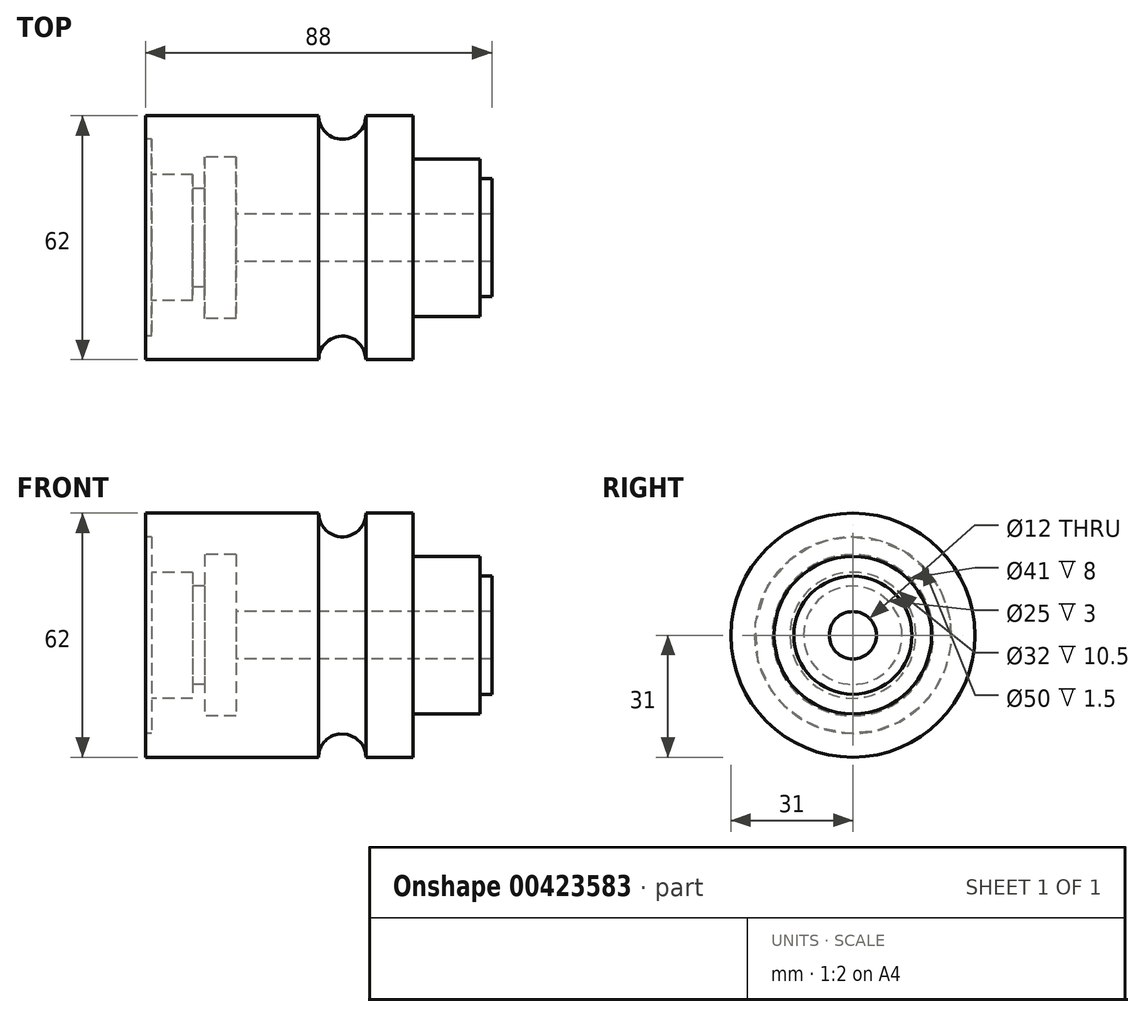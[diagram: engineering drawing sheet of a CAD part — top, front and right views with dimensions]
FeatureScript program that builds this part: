
annotation { "Feature Type Name" : "Feature", "Feature Type Description" : "" }
export const myFeature = defineFeature(function(context is Context, id is Id, definition is map)
    precondition{}
    {
        {
            var Q0;
            Q0=qCreatedBy(makeId("Front.planeOp"),FACE);
            var sketch = newSketch(context, id + "F0", { "sketchPlane" : qUnion([Q0])});
            skLineSegment(sketch, "E0", {"start": v(0, 0) * mm, "end": v(227.58, 0) * mm, "construction": true});
            skLineSegment(sketch, "E1", {"start": v(0, 0) * mm, "end": v(0, 31) * mm});
            skLineSegment(sketch, "E2", {"start": v(0, 31) * mm, "end": v(44, 31) * mm});
            skLineSegment(sketch, "E3", {"start": v(68, 31) * mm, "end": v(68, 20) * mm});
            skLineSegment(sketch, "E4", {"start": v(68, 20) * mm, "end": v(85, 20) * mm});
            skLineSegment(sketch, "E5", {"start": v(85, 20) * mm, "end": v(85, 15) * mm});
            skLineSegment(sketch, "E6", {"start": v(85, 15) * mm, "end": v(88, 15) * mm});
            skLineSegment(sketch, "E7", {"start": v(88, 15) * mm, "end": v(88, 0) * mm});
            skLineSegment(sketch, "E8", {"start": v(88, 0) * mm, "end": v(0, 0) * mm});
            skArc(sketch, "E9", {"start": v(44, 31) * mm, "mid": v(50, 25) * mm, "end": v(56, 31) * mm});
            skLineSegment(sketch, "E10.trimOffspring", {"start": v(56, 31) * mm, "end": v(68, 31) * mm});
            skSolve(sketch);
        }
        {
            var Q0;
            Q0=makeQuery(id+"F0.imprint","IMPRINT",FACE,{"disambiguationData":[TD([[makeQuery(id+"F0.imprint","IMPRINT",EDGE,{"derivedFrom":sQuery(id+"F0.wireOp",EDGE,"E1")}),-1.0]])]});
            var Q1;
            Q1=sQuery(id+"F0.wireOp",EDGE,"E0");
            revolve(context, id + "F1", {"entities" : qUnion([Q0]), "axis" : qUnion([Q1]), "revolveType" : RevolveType.FULL});
        }
        {
            var Q0;
            Q0=qCreatedBy(makeId("Front.planeOp"),FACE);
            var sketch = newSketch(context, id + "F2", { "sketchPlane" : qUnion([Q0])});
            skLineSegment(sketch, "E11", {"start": v(0, 0) * mm, "end": v(122.44, 0) * mm, "construction": true});
            skLineSegment(sketch, "E12", {"start": v(0, 0) * mm, "end": v(0, 25) * mm});
            skLineSegment(sketch, "E13", {"start": v(0, 25) * mm, "end": v(1.5, 25) * mm});
            skLineSegment(sketch, "E14", {"start": v(1.5, 25) * mm, "end": v(1.5, 16) * mm});
            skLineSegment(sketch, "E15", {"start": v(1.5, 16) * mm, "end": v(12, 16) * mm});
            skLineSegment(sketch, "E16", {"start": v(12, 16) * mm, "end": v(12, 12.5) * mm});
            skLineSegment(sketch, "E17", {"start": v(12, 12.5) * mm, "end": v(15, 12.5) * mm});
            skLineSegment(sketch, "E18", {"start": v(15, 12.5) * mm, "end": v(15, 20.5) * mm});
            skLineSegment(sketch, "E19", {"start": v(15, 20.5) * mm, "end": v(23, 20.5) * mm});
            skLineSegment(sketch, "E20", {"start": v(23, 20.5) * mm, "end": v(23, 6) * mm});
            skLineSegment(sketch, "E21", {"start": v(23, 6) * mm, "end": v(93, 6) * mm});
            skLineSegment(sketch, "E22", {"start": v(93, 6) * mm, "end": v(93, 0) * mm});
            skLineSegment(sketch, "E23", {"start": v(93, 0) * mm, "end": v(0, 0) * mm});
            skSolve(sketch);
        }
        {
            var Q0;
            Q0=makeQuery(id+"F2.imprint","IMPRINT",FACE,{"disambiguationData":[TD([[makeQuery(id+"F2.imprint","IMPRINT",EDGE,{"derivedFrom":sQuery(id+"F2.wireOp",EDGE,"E12")}),-1.0]])]});
            var Q1;
            Q1=sQuery(id+"F2.wireOp",EDGE,"E23");
            revolve(context, id + "F3", {"operationType" : NewBodyOperationType.REMOVE, "entities" : qUnion([Q0]), "axis" : qUnion([Q1]), "revolveType" : RevolveType.FULL, "oppositeDirection" : true});
        }
    });
